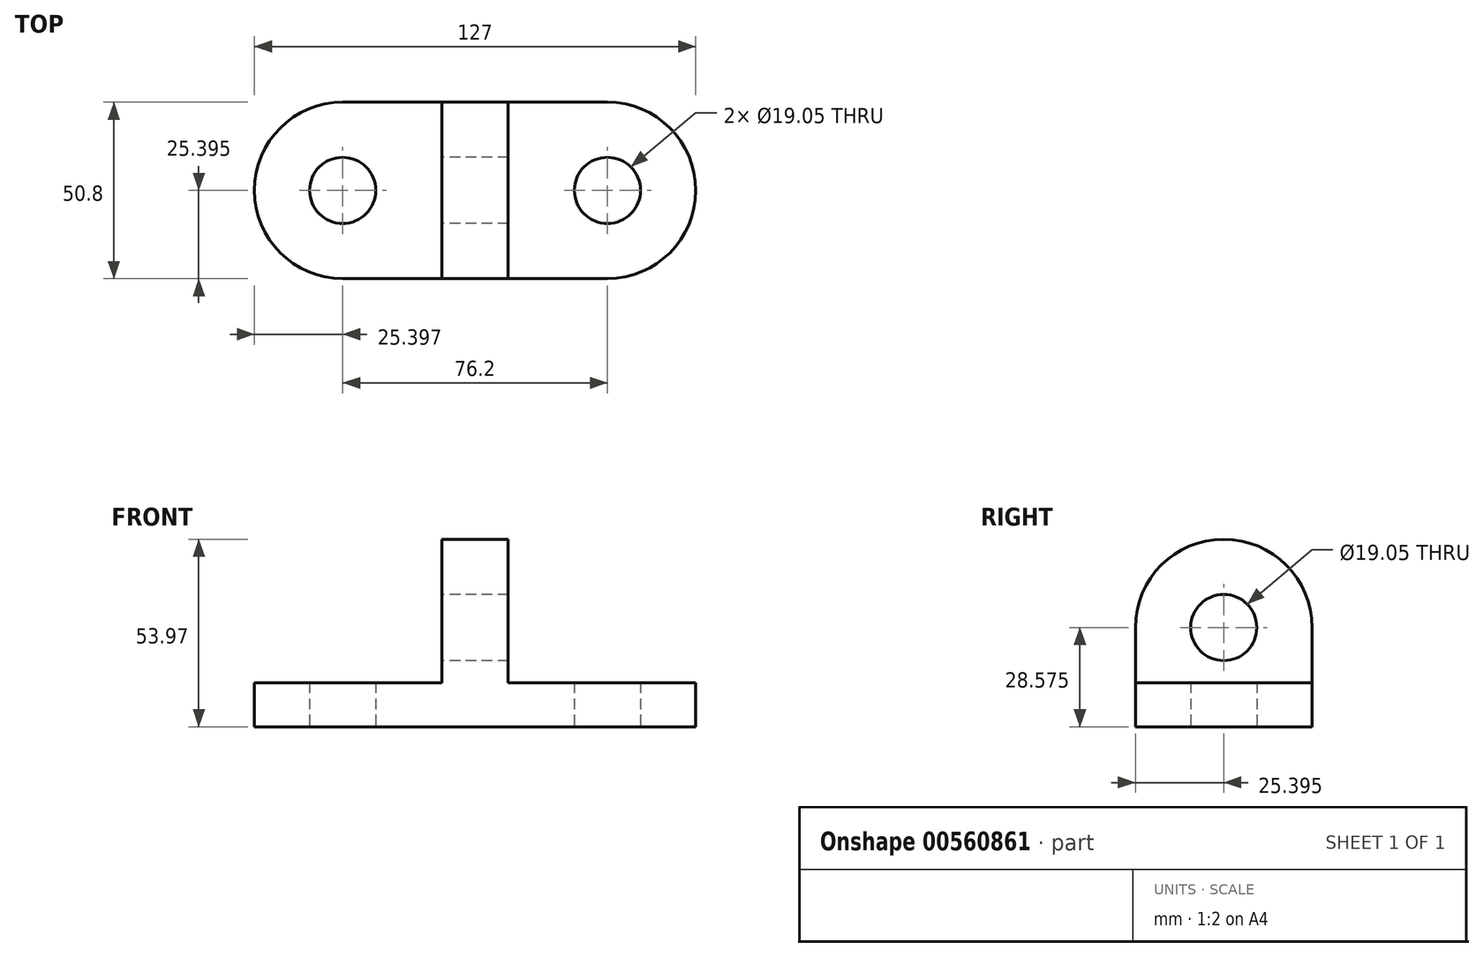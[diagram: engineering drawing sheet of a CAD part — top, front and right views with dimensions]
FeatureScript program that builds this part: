
annotation { "Feature Type Name" : "Feature", "Feature Type Description" : "" }
export const myFeature = defineFeature(function(context is Context, id is Id, definition is map)
    precondition{}
    {
        {
            var Q0;
            Q0=qCreatedBy(makeId("Top.planeOp"),FACE);
            var sketch = newSketch(context, id + "F0", { "sketchPlane" : qUnion([Q0])});
            skLineSegment(sketch, "E0.bottom", {"start": v(-39.73, 20.92) * mm, "end": v(36.47, 20.92) * mm});
            skLineSegment(sketch, "E0.top", {"start": v(-39.73, -29.88) * mm, "end": v(36.47, -29.88) * mm});
            skLineSegment(sketch, "E0.left", {"start": v(-39.73, 20.92) * mm, "end": v(-39.73, -29.88) * mm});
            skLineSegment(sketch, "E0.right", {"start": v(36.47, 20.92) * mm, "end": v(36.47, -29.88) * mm});
            skArc(sketch, "E1", {"start": v(-39.73, 20.92) * mm, "mid": v(-65.13, -4.48) * mm, "end": v(-39.73, -29.88) * mm});
            skArc(sketch, "E2", {"start": v(36.47, -29.88) * mm, "mid": v(61.87, -4.48) * mm, "end": v(36.47, 20.92) * mm});
            skCircle(sketch, "E3", {"center": v(-39.73, -4.48) * mm, "radius": 9.53 * mm});
            skCircle(sketch, "E4", {"center": v(36.47, -4.48) * mm, "radius": 9.53 * mm});
            skSolve(sketch);
        }
        {
            var Q0;
            {var subQ5=sQuery(id+"F0.wireOp",EDGE,"E0.bottom");Q0=makeQuery(id+"F0.imprint","IMPRINT",FACE,{"disambiguationData":[TD([[makeQuery(id+"F0.imprint","IMPRINT",EDGE,{"derivedFrom":subQ5}),-1.0]])]});}
            var Q1;
            {var subQ0=sQuery(id+"F0.wireOp",EDGE,"E1");Q1=makeQuery(id+"F0.imprint","IMPRINT",FACE,{"disambiguationData":[TD([[makeQuery(id+"F0.imprint","IMPRINT",EDGE,{"derivedFrom":subQ0}),1.0]])]});}
            var Q2;
            {var subQ0=sQuery(id+"F0.wireOp",EDGE,"E2");Q2=makeQuery(id+"F0.imprint","IMPRINT",FACE,{"disambiguationData":[TD([[makeQuery(id+"F0.imprint","IMPRINT",EDGE,{"derivedFrom":subQ0}),1.0]])]});}
            extrude(context, id + "F1", {"entities" : qUnion([Q0, Q1, Q2]), "depth" : 12.7 * mm, "offsetDistance" : 25.4 * mm});
        }
        {
            var Q0;
            Q0=makeQuery(id+"F1.opExtrude","CAP_FACE",FACE,{"disambiguationData":[OSD([sQuery(id+"F0.wireOp",EDGE,"E0.bottom"),sQuery(id+"F0.wireOp",EDGE,"E0.top"),sQuery(id+"F0.wireOp",EDGE,"E1"),sQuery(id+"F0.wireOp",EDGE,"E2"),sQuery(id+"F0.wireOp",EDGE,"E3"),sQuery(id+"F0.wireOp",EDGE,"E4")])],"isStart":false});
            var sketch = newSketch(context, id + "F2", { "sketchPlane" : qUnion([Q0])});
            skLineSegment(sketch, "E5.bottom", {"start": v(-11.16, 20.92) * mm, "end": v(7.9, 20.92) * mm});
            skLineSegment(sketch, "E5.top", {"start": v(-11.16, -29.88) * mm, "end": v(7.9, -29.88) * mm});
            skLineSegment(sketch, "E5.left", {"start": v(-11.16, 20.92) * mm, "end": v(-11.16, -29.88) * mm});
            skLineSegment(sketch, "E5.right", {"start": v(7.9, 20.92) * mm, "end": v(7.9, -29.88) * mm});
            skSolve(sketch);
        }
        {
            var Q0;
            Q0=makeQuery(id+"F2.imprint","IMPRINT",FACE,{"disambiguationData":[TD([[makeQuery(id+"F2.imprint","IMPRINT",EDGE,{"derivedFrom":sQuery(id+"F2.wireOp",EDGE,"E5.bottom")}),-1.0]])]});
            extrude(context, id + "F3", {"entities" : qUnion([Q0]), "operationType" : NewBodyOperationType.ADD, "depth" : 15.88 * mm, "offsetDistance" : 25.4 * mm});
        }
        {
            var Q0;
            Q0=makeQuery(id+"F3.opExtrude","SWEPT_FACE",FACE,{"disambiguationData":[OSD([sQuery(id+"F2.wireOp",EDGE,"E5.left")])]});
            var sketch = newSketch(context, id + "F4", { "sketchPlane" : qUnion([Q0])});
            skArc(sketch, "E6", {"start": v(29.88, 28.58) * mm, "mid": v(4.48, 53.98) * mm, "end": v(-20.92, 28.58) * mm});
            skSolve(sketch);
        }
        {
            var Q0;
            Q0=makeQuery(id+"F4.imprint","IMPRINT",FACE,{"disambiguationData":[TD([[makeQuery(id+"F4.imprint","IMPRINT",EDGE,{"derivedFrom":sQuery(id+"F4.wireOp",EDGE,"E6")}),1.0]])]});
            extrude(context, id + "F5", {"entities" : qUnion([Q0]), "operationType" : NewBodyOperationType.ADD, "oppositeDirection" : true, "depth" : 19.05 * mm, "offsetDistance" : 25.4 * mm});
        }
        {
            var Q0;
            {var subQ0=sQuery(id+"F2.wireOp",EDGE,"E5.left");Q0=makeQuery(id+"F5.boolean.opBoolean","MERGE",FACE,{"derivedFrom":[makeQuery(id+"F3.opExtrude","SWEPT_FACE",FACE,{"disambiguationData":[OSD([subQ0])]}),makeQuery(id+"F5.opExtrude","CAP_FACE",FACE,{"disambiguationData":[OSD([subQ0,sQuery(id+"F4.wireOp",EDGE,"E6")])],"isStart":true})]});}
            var sketch = newSketch(context, id + "F6", { "sketchPlane" : qUnion([Q0])});
            skCircle(sketch, "E7", {"center": v(4.48, 28.58) * mm, "radius": 9.53 * mm});
            skSolve(sketch);
        }
        {
            var Q0;
            Q0=makeQuery(id+"F6.imprint","IMPRINT",FACE,{"disambiguationData":[TD([[makeQuery(id+"F6.imprint","IMPRINT",EDGE,{"derivedFrom":sQuery(id+"F6.wireOp",EDGE,"E7")}),1.0]])]});
            extrude(context, id + "F7", {"entities" : qUnion([Q0]), "operationType" : NewBodyOperationType.REMOVE, "oppositeDirection" : true, "depth" : 19.05 * mm, "offsetDistance" : 25.4 * mm});
        }
    });
